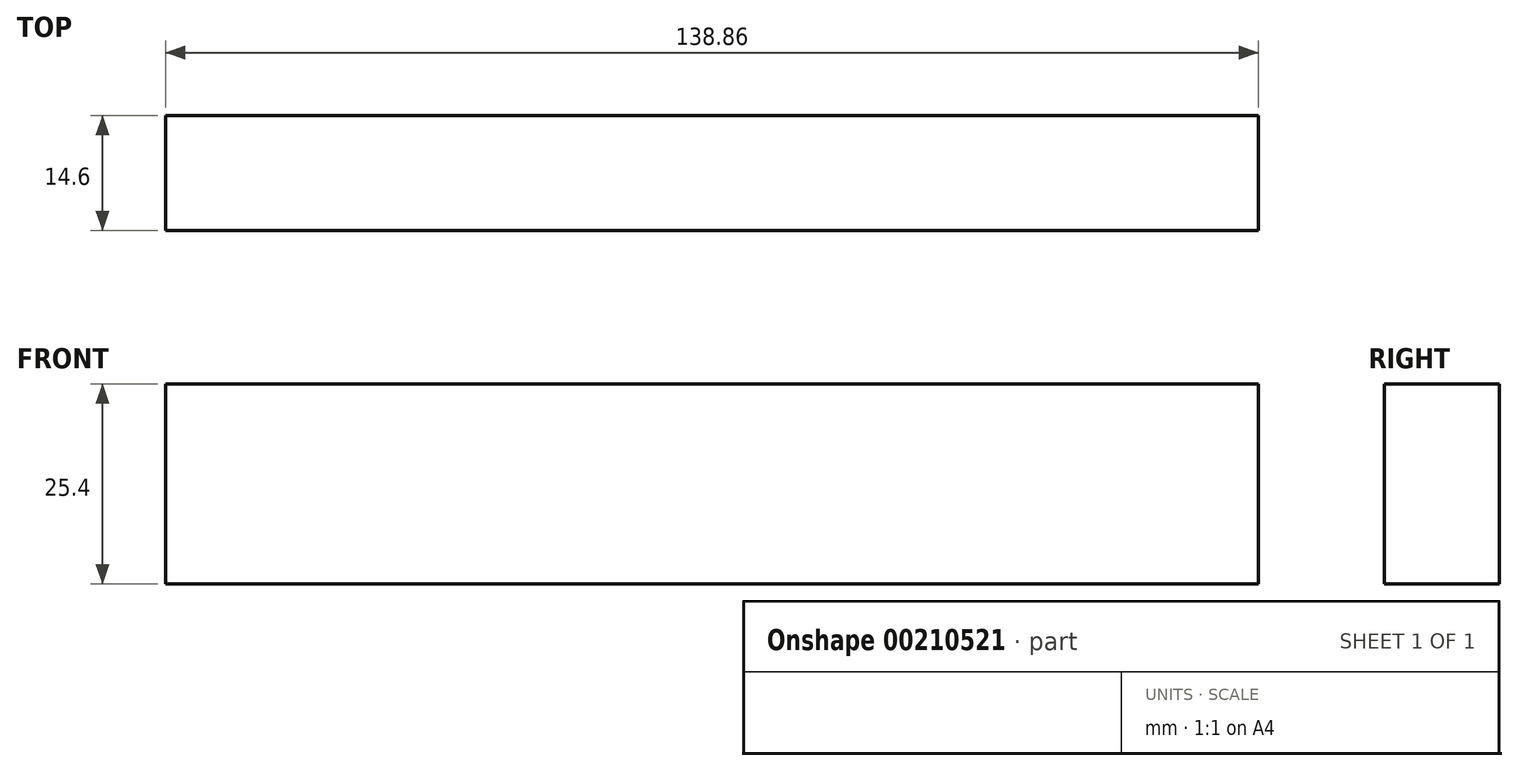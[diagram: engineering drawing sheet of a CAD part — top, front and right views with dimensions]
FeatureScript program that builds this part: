
annotation { "Feature Type Name" : "Feature", "Feature Type Description" : "" }
export const myFeature = defineFeature(function(context is Context, id is Id, definition is map)
    precondition{}
    {
        {
            var Q0;
            Q0=qCreatedBy(makeId("Top.planeOp"),FACE);
            var sketch = newSketch(context, id + "F0", { "sketchPlane" : qUnion([Q0])});
            skLineSegment(sketch, "E0", {"start": v(-70.92, 7.3) * mm, "end": v(-70.92, -7.3) * mm});
            skLineSegment(sketch, "E1", {"start": v(-70.92, 7.3) * mm, "end": v(67.94, 7.3) * mm});
            skLineSegment(sketch, "E2", {"start": v(67.94, 7.3) * mm, "end": v(67.94, -7.3) * mm});
            skLineSegment(sketch, "E3", {"start": v(67.94, -7.3) * mm, "end": v(-70.92, -7.3) * mm});
            skSolve(sketch);
        }
        {
            var Q0;
            Q0=makeQuery(id+"F0.imprint","IMPRINT",FACE,{"disambiguationData":[TD([[makeQuery(id+"F0.imprint","IMPRINT",EDGE,{"derivedFrom":sQuery(id+"F0.wireOp",EDGE,"E0")}),1.0]])]});
            extrude(context, id + "F1", {"entities" : qUnion([Q0]), "depth" : 25.4 * mm});
        }
    });
